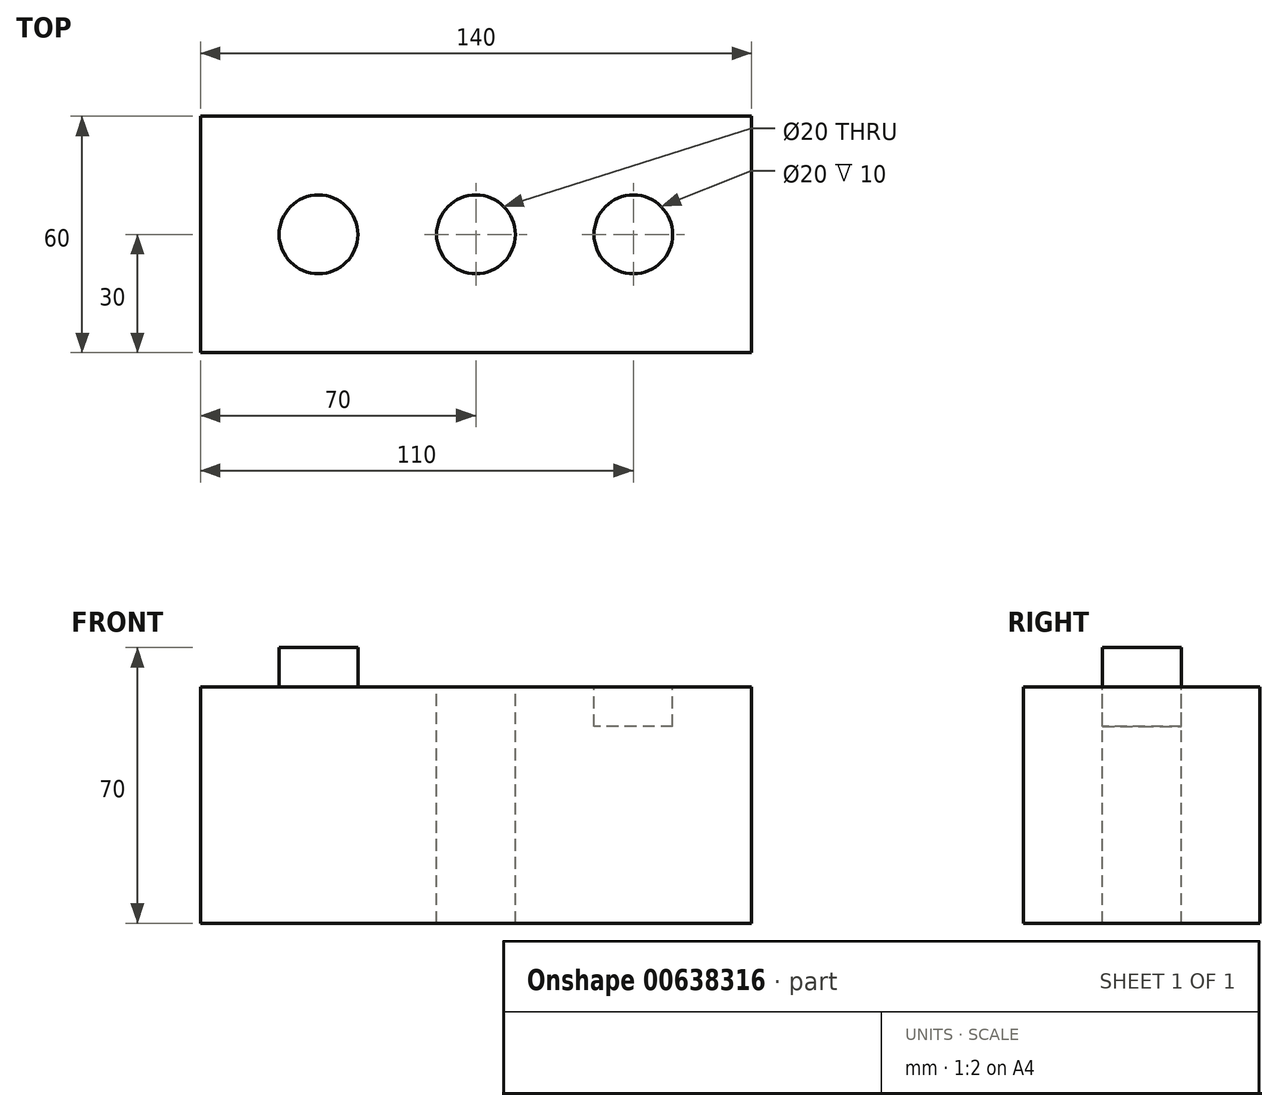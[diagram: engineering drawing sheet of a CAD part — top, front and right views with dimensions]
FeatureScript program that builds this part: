
annotation { "Feature Type Name" : "Feature", "Feature Type Description" : "" }
export const myFeature = defineFeature(function(context is Context, id is Id, definition is map)
    precondition{}
    {
        {
            var Q0;
            Q0=qCreatedBy(makeId("Top.planeOp"),FACE);
            var sketch = newSketch(context, id + "F0", { "sketchPlane" : qUnion([Q0])});
            skLineSegment(sketch, "E0.bottom", {"start": v(-70, 30) * mm, "end": v(70, 30) * mm});
            skLineSegment(sketch, "E0.top", {"start": v(-70, -30) * mm, "end": v(70, -30) * mm});
            skLineSegment(sketch, "E0.left", {"start": v(-70, 30) * mm, "end": v(-70, -30) * mm});
            skLineSegment(sketch, "E0.right", {"start": v(70, 30) * mm, "end": v(70, -30) * mm});
            skPoint(sketch, "E0.middle", {"position": v(0, 0) * mm});
            skSolve(sketch);
        }
        {
            var Q0;
            Q0 = qSketchRegion(id + "F0", true);
            extrude(context, id + "F1", {"entities" : qUnion([Q0]), "depth" : 60 * mm, "offsetDistance" : 25 * mm});
        }
        {
            var Q0;
            Q0=makeQuery(id+"F1.opExtrude","CAP_FACE",FACE,{"disambiguationData":[OSD([sQuery(id+"F0.wireOp",EDGE,"E0.bottom"),sQuery(id+"F0.wireOp",EDGE,"E0.top"),sQuery(id+"F0.wireOp",EDGE,"E0.left"),sQuery(id+"F0.wireOp",EDGE,"E0.right")])],"isStart":false});
            var sketch = newSketch(context, id + "F2", { "sketchPlane" : qUnion([Q0])});
            skCircle(sketch, "E1", {"center": v(-40, 0) * mm, "radius": 10 * mm});
            skSolve(sketch);
        }
        {
            var Q0;
            Q0=makeQuery(id+"F2.imprint","IMPRINT",FACE,{"disambiguationData":[TD([[makeQuery(id+"F2.imprint","IMPRINT",EDGE,{"derivedFrom":sQuery(id+"F2.wireOp",EDGE,"E1")}),-1.0]])]});
            var sketch = newSketch(context, id + "F3", { "sketchPlane" : qUnion([Q0])});
            skCircle(sketch, "E2", {"center": v(0, 0) * mm, "radius": 10 * mm});
            skSolve(sketch);
        }
        {
            var Q0;
            Q0=makeQuery(id+"F2.imprint","IMPRINT",FACE,{"disambiguationData":[TD([[makeQuery(id+"F2.imprint","IMPRINT",EDGE,{"derivedFrom":sQuery(id+"F2.wireOp",EDGE,"E1")}),-1.0]])]});
            var sketch = newSketch(context, id + "F4", { "sketchPlane" : qUnion([Q0])});
            skCircle(sketch, "E3", {"center": v(40, 0) * mm, "radius": 10 * mm});
            skSolve(sketch);
        }
        {
            var Q0;
            Q0 = qSketchRegion(id + "F2", true);
            extrude(context, id + "F5", {"entities" : qUnion([Q0]), "operationType" : NewBodyOperationType.ADD, "depth" : 10 * mm, "offsetDistance" : 25 * mm});
        }
        {
            var Q0;
            Q0 = qSketchRegion(id + "F3", true);
            extrude(context, id + "F6", {"entities" : qUnion([Q0]), "operationType" : NewBodyOperationType.REMOVE, "oppositeDirection" : true, "depth" : 95.9 * mm, "offsetDistance" : 25 * mm});
        }
        {
            var Q0;
            Q0 = qSketchRegion(id + "F4", true);
            extrude(context, id + "F7", {"entities" : qUnion([Q0]), "operationType" : NewBodyOperationType.REMOVE, "oppositeDirection" : true, "depth" : 10 * mm, "offsetDistance" : 25 * mm});
        }
    });
